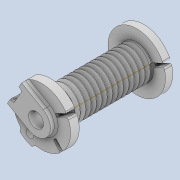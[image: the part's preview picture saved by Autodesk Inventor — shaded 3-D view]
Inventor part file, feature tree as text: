
AUTODESK INVENTOR PART (.ipt)
format: ipt  version: 2020 (Build 240168000, 168)  size: 1,140,224 bytes
history: native  units: mm
features: sketch x14, other x3, plane x1
ambient origin geometry x8: Origin, YZ Plane, XZ Plane, XY Plane, X Axis, Y Axis, Z Axis, Center Point
bodies: Solid1 (feature_tree)
feature tree (18):
  other  "cab_coil_1.ipt"
  other  "Solid1::cab_coil_1.ipt"
  other  "TaggingFeature1"
  sketch  "Sketch1"  dims[d0=10.0mm]
  sketch  "Sketch2"
  sketch  "Sketch3"
  sketch  "Sketch4"
  sketch  "Sketch5"
  sketch  "Sketch6"
  sketch  "Sketch7"
  sketch  "Sketch8"
  sketch  "Sketch9"
  sketch  "Sketch10"
  sketch  "Sketch11"
  sketch  "Sketch12"
  sketch  "Sketch14"
  sketch  "3D Sketch1"
  plane  "Work Plane1"
